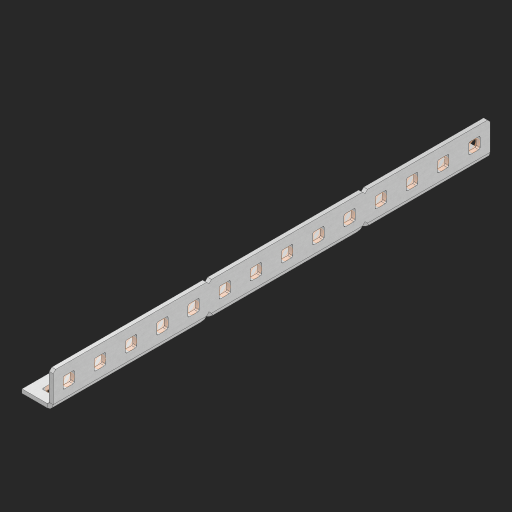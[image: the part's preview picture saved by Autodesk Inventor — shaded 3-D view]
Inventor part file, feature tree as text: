
AUTODESK INVENTOR PART (.ipt)
format: ipt  version: 2023 (Build 270158000, 158)  size: 570,368 bytes
history: native  units: in
note: dims shown in document units (in); Inventor stores cm internally (conversion verified against a paired STEP export)
features: other x33, extrude x27, sheet_metal_op x10, sketch x8, mirror x1, pattern_linear x1, chamfer x1
ambient origin geometry x8: Origin, YZ Plane, XZ Plane, XY Plane, X Axis, Y Axis, Z Axis, Center Point
bodies: Solid1 (feature_tree), Body (feature_tree)
feature tree (81):
  other  "Flange Pattern Plane"
  sheet_metal_op  "Flange Pattern"
  sheet_metal_op  "Body Pattern"
  other  "Arc Length"
  mirror  "Notch Mirror"
  pattern_linear  "Notch Pattern"  Spacing1=0.25in  [1 undecoded]
  chamfer  "End Chamfer"
  extrude  "Half Cut"  Depth=0.0625in
  sketch  "Sketch1"  dims[d0=1.5in]
  other  "Plate1"
  sketch  "Sketch2"  dims[d1=7.0in]
  other  "Plate2"
  sheet_metal_op  "Bend1"
  sheet_metal_op  "Corner1"
  sketch  "Sketch3"  dims[d2=0.0625in]
  other  "Flange Pattern Sketch"
  sketch  "Sketch7"  dims[d3=0.0625in]
  other  "Srf1"
  other  "Srf2"
  sketch  "Sketch8"  dims[d4=0.0312in]
  sketch  "Sketch9"  dims[d5=0.125in]
  other  "Srf91"
  sheet_metal_op  "Body Pattern Sketch"
  other  "Srf92"
  sketch  "Sketch13"  dims[d6=0.0625in]
  sketch  "Sketch14"  dims[d7=0.5in d8=90.0deg d9=0.0312in d10=0.25in d11=0.0625in d12=0.0625in d16=0.182in d17=0.02in d18=0.0625in d19=0.0in d20=0.25in d21=0.25in d46=0.172in d47=1.0in d48=0.0in d49=0.182in d50=0.02in d51=0.25in d52=0.25in d53=0.0625in d54=0.0in d55=0.172in d56=1.0in d57=0.0in d60=5.5118in d62=0.5in d63=0.3937in d65=0.5in d85=0.1473in d86=0.1782in d88=0.04in d89=0.0625in d90=0.0in d91=0.04in d92=0.0491in d95=2.5in d96=0.04in d97=0.25in d98=45.0deg d101=0.0in d102=2.497in d131=0.5in d132=5.5118in d134=0.5in d139=0.5in]
  other  "Srf856"
  other  "Srf1310"
  other  "Srf1311"
  other  "Srf1312"
  other  "Srf1376"
  other  "Srf1377"
  other  "Srf1728"
  other  "Srf1755"
  other  "Srf1878"
  other  "Srf1879"
  other  "Srf1880"
  other  "Srf1881"
  other  "Srf1882"
  other  "Srf1883"
  other  "Srf1884"
  other  "Srf1885"
  other  "Srf1942"
  other  "Srf1943"
  other  "Srf1944"
  other  "Srf1945"
  other  "Srf1946"
  other  "Srf1947"
  other  "Srf1948"
  other  "Srf1949"
  sheet_metal_op  "Flange Stamp"
  sheet_metal_op  "Flange Circle"
  sheet_metal_op  "Body Stamp"
  sheet_metal_op  "Body Circle"
  sheet_metal_op  "Notch"
  extrude  "ExtrusionSrf2"  Depth=0.0625in
  extrude  "ExtrusionSrf92"  Depth=0.5in
  extrude  "ExtrusionSrf856"  Depth=0.02in
  extrude  "ExtrusionSrf1310"  Depth=0.0625in
  extrude  "ExtrusionSrf1311"  TaperAngle=0.0deg  [1 undecoded]
  extrude  "ExtrusionSrf1312"  Depth=0.5in
  extrude  "ExtrusionSrf1376"  Depth=0.5in
  extrude  "ExtrusionSrf1377"  Depth=0.5in
  extrude  "ExtrusionSrf1728"  Depth=0.5in TaperAngle=0.0deg
  extrude  "ExtrusionSrf1755"  Depth=0.5in
  extrude  "ExtrusionSrf1878"  Depth=0.02in
  extrude  "ExtrusionSrf1879"  Depth=0.5in
  extrude  "ExtrusionSrf1880"  Depth=0.5in
  extrude  "ExtrusionSrf1881"  Depth=0.0625in
  extrude  "ExtrusionSrf1882"  TaperAngle=0.0deg  [1 undecoded]
  extrude  "ExtrusionSrf1883"  Depth=0.5in
  extrude  "ExtrusionSrf1884"  Depth=0.5in TaperAngle=0.0deg
  extrude  "ExtrusionSrf1885"  Depth=0.5in
  extrude  "ExtrusionSrf1942"  Depth=0.5in
  extrude  "ExtrusionSrf1943"  Depth=0.5in
  extrude  "ExtrusionSrf1944"  Depth=0.5in
  extrude  "ExtrusionSrf1945"  Depth=0.5in
  extrude  "ExtrusionSrf1946"  Depth=0.0625in
  extrude  "ExtrusionSrf1947"  TaperAngle=0.0deg  [1 undecoded]
  extrude  "ExtrusionSrf1948"  Depth=0.5in
  extrude  "ExtrusionSrf1949"  Depth=0.5in
note: 4 required parameter values undecoded (feature->parameter linkage not recoverable at this tier; creation-order binding heuristic only, values carry confidence <= 0.55)
